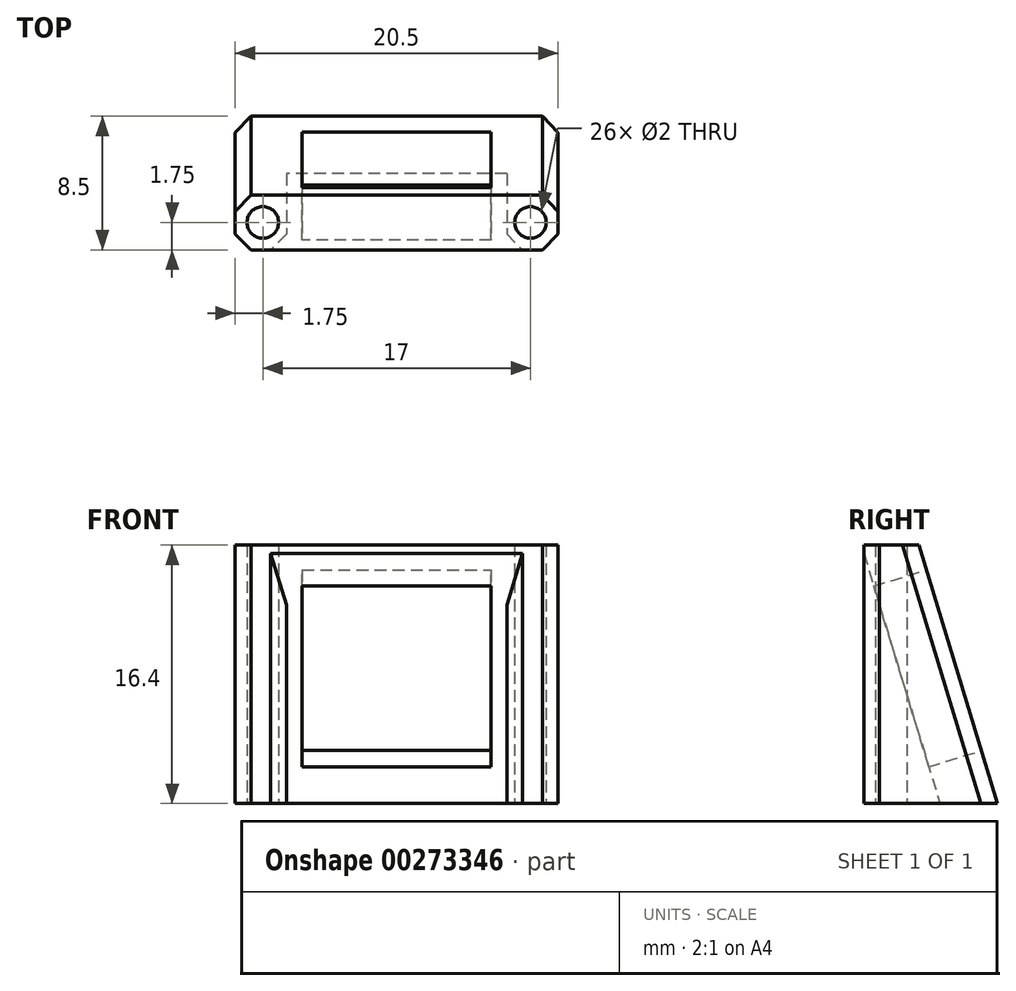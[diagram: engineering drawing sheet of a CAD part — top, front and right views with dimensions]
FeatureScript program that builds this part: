
annotation { "Feature Type Name" : "Feature", "Feature Type Description" : "" }
export const myFeature = defineFeature(function(context is Context, id is Id, definition is map)
    precondition{}
    {
        {
            var Q0;
            Q0=qCreatedBy(makeId("Top.planeOp"),FACE);
            var sketch = newSketch(context, id + "F0", { "sketchPlane" : qUnion([Q0])});
            skLineSegment(sketch, "E0.bottom", {"start": v(10.25, 4.25) * mm, "end": v(-10.25, 4.25) * mm});
            skLineSegment(sketch, "E0.top", {"start": v(10.25, -4.25) * mm, "end": v(-10.25, -4.25) * mm});
            skLineSegment(sketch, "E0.left", {"start": v(10.25, 4.25) * mm, "end": v(10.25, -4.25) * mm});
            skLineSegment(sketch, "E0.right", {"start": v(-10.25, 4.25) * mm, "end": v(-10.25, -4.25) * mm});
            skPoint(sketch, "E0.middle", {"position": v(0, 0) * mm});
            skCircle(sketch, "E1", {"center": v(-8.5, -2.5) * mm, "radius": 1 * mm});
            skCircle(sketch, "E2", {"center": v(8.5, -2.5) * mm, "radius": 1 * mm});
            skLineSegment(sketch, "E3", {"start": v(-8.5, -2.5) * mm, "end": v(8.5, -2.5) * mm});
            skLineSegment(sketch, "E4", {"start": v(0, 0) * mm, "end": v(0, -2.5) * mm});
            skSolve(sketch);
        }
        {
            var Q0;
            Q0=makeQuery(id+"F0.imprint","IMPRINT",FACE,{"disambiguationData":[TD([[makeQuery(id+"F0.imprint","IMPRINT",EDGE,{"derivedFrom":sQuery(id+"F0.wireOp",EDGE,"E0.bottom")}),1.0]])]});
            extrude(context, id + "F1", {"entities" : qUnion([Q0]), "depth" : 16.4 * mm});
        }
        {
            var Q0;
            Q0=makeQuery(id+"F1.opExtrude","CAP_EDGE",EDGE,{"disambiguationData":[OSD([sQuery(id+"F0.wireOp",EDGE,"E0.bottom")])],"isStart":false});
            chamfer(context, id + "F2", {"entities" : qUnion([Q0]), "chamferType" : ChamferType.TWO_OFFSETS, "width1" : 5 * mm, "oppositeDirection" : false, "width2" : 16.4 * mm, "tangentPropagation" : true});
        }
        {
            var Q0;
            Q0=makeQuery(id+"F2.opChamfer","BLEND_FACE",FACE,{"disambiguationData":[OSD([sQuery(id+"F0.wireOp",EDGE,"E0.bottom")])]});
            var sketch = newSketch(context, id + "F3", { "sketchPlane" : qUnion([Q0])});
            skLineSegment(sketch, "E5.bottom", {"start": v(6, 14.26) * mm, "end": v(-6, 14.26) * mm});
            skLineSegment(sketch, "E5.top", {"start": v(6, 2.26) * mm, "end": v(-6, 2.26) * mm});
            skLineSegment(sketch, "E5.left", {"start": v(6, 14.26) * mm, "end": v(6, 2.26) * mm});
            skLineSegment(sketch, "E5.right", {"start": v(-6, 14.26) * mm, "end": v(-6, 2.26) * mm});
            skPoint(sketch, "E5.middle", {"position": v(0, 8.26) * mm});
            skLineSegment(sketch, "E6.0", {"start": v(10.25, 15.9) * mm, "end": v(10.25, -1.24) * mm});
            skSolve(sketch);
        }
        {
            var Q0;
            {var subQ3=sQuery(id+"F3.wireOp",EDGE,"E5.bottom");Q0=makeQuery(id+"F3.imprint","IMPRINT",FACE,{"disambiguationData":[TD([[makeQuery(id+"F3.imprint","IMPRINT",EDGE,{"derivedFrom":subQ3}),1.0]])]});}
            extrude(context, id + "F4", {"entities" : qUnion([Q0]), "operationType" : NewBodyOperationType.REMOVE, "endBound" : BoundingType.THROUGH_ALL, "oppositeDirection" : true, "depth" : 25 * mm});
        }
        {
            var Q0;
            Q0=makeQuery(id+"F2.opChamfer","BLEND_FACE",FACE,{"disambiguationData":[OSD([sQuery(id+"F0.wireOp",EDGE,"E0.bottom")])]});
            cPlane(context, id + "F5", {"entities" : qUnion([Q0]), "cplaneType" : CPlaneType.OFFSET, "offset" : 8.5 * mm, "oppositeDirection" : true, "width" : 150 * mm, "height" : 150 * mm});
        }
        {
            var Q0;
            Q0=qCreatedBy(id+"F5.planeOp",FACE);
            var sketch = newSketch(context, id + "F6", { "sketchPlane" : qUnion([Q0])});
            skLineSegment(sketch, "E7.bottom", {"start": v(7, 18.45) * mm, "end": v(-7, 18.45) * mm});
            skLineSegment(sketch, "E7.top", {"start": v(7, -1.55) * mm, "end": v(-7, -1.55) * mm});
            skLineSegment(sketch, "E7.left", {"start": v(7, 18.45) * mm, "end": v(7, -1.55) * mm});
            skLineSegment(sketch, "E7.right", {"start": v(-7, 18.45) * mm, "end": v(-7, -1.55) * mm});
            skPoint(sketch, "E7.middle", {"position": v(0, 8.45) * mm});
            skSolve(sketch);
        }
        {
            var Q0;
            Q0=makeQuery(id+"F6.imprint","IMPRINT",FACE,{"disambiguationData":[TD([[makeQuery(id+"F6.imprint","IMPRINT",EDGE,{"derivedFrom":sQuery(id+"F6.wireOp",EDGE,"E7.bottom")}),1.0]])]});
            extrude(context, id + "F7", {"entities" : qUnion([Q0]), "operationType" : NewBodyOperationType.REMOVE, "depth" : 5 * mm});
        }
        {
            var Q0;
            Q0=makeQuery(id+"F2.opChamfer","BLEND_EDGE",EDGE,{"blendedFrom":[makeQuery(id+"F1.opExtrude","CAP_EDGE",EDGE,{"disambiguationData":[OSD([sQuery(id+"F0.wireOp",EDGE,"E0.bottom")])],"isStart":false}),makeQuery(id+"F1.opExtrude","SWEPT_FACE",FACE,{"disambiguationData":[OSD([sQuery(id+"F0.wireOp",EDGE,"E0.right")])]})],"blendedInto":[makeQuery(id+"F1.opExtrude","SWEPT_FACE",FACE,{"disambiguationData":[OSD([sQuery(id+"F0.wireOp",EDGE,"E0.right")])]})]});
            var Q1;
            Q1=makeQuery(id+"F1.opExtrude","SWEPT_EDGE",EDGE,{"disambiguationData":[OSD([sQuery(id+"F0.wireOp",EDGE,"E0.top"),sQuery(id+"F0.wireOp",EDGE,"E0.right")])]});
            var Q2;
            Q2=makeQuery(id+"F2.opChamfer","BLEND_EDGE",EDGE,{"blendedFrom":[makeQuery(id+"F1.opExtrude","CAP_EDGE",EDGE,{"disambiguationData":[OSD([sQuery(id+"F0.wireOp",EDGE,"E0.bottom")])],"isStart":false}),makeQuery(id+"F1.opExtrude","SWEPT_FACE",FACE,{"disambiguationData":[OSD([sQuery(id+"F0.wireOp",EDGE,"E0.left")])]})],"blendedInto":[makeQuery(id+"F1.opExtrude","SWEPT_FACE",FACE,{"disambiguationData":[OSD([sQuery(id+"F0.wireOp",EDGE,"E0.left")])]})]});
            var Q3;
            Q3=makeQuery(id+"F1.opExtrude","SWEPT_EDGE",EDGE,{"disambiguationData":[OSD([sQuery(id+"F0.wireOp",EDGE,"E0.top"),sQuery(id+"F0.wireOp",EDGE,"E0.left")])]});
            var Q4;
            Q4=makeQuery(id+"F7.boolean.opBoolean","INTERSECT",EDGE,{"derivedFrom":[makeQuery(id+"F1.opExtrude","SWEPT_FACE",FACE,{"disambiguationData":[OSD([sQuery(id+"F0.wireOp",EDGE,"E0.top")])]}),makeQuery(id+"F7.opExtrude","SWEPT_FACE",FACE,{"disambiguationData":[OSD([sQuery(id+"F6.wireOp",EDGE,"E7.right")])]})]});
            var Q5;
            Q5=makeQuery(id+"F7.boolean.opBoolean","INTERSECT",EDGE,{"derivedFrom":[makeQuery(id+"F1.opExtrude","SWEPT_FACE",FACE,{"disambiguationData":[OSD([sQuery(id+"F0.wireOp",EDGE,"E0.top")])]}),makeQuery(id+"F7.opExtrude","SWEPT_FACE",FACE,{"disambiguationData":[OSD([sQuery(id+"F6.wireOp",EDGE,"E7.left")])]})]});
            chamfer(context, id + "F8", {"entities" : qUnion([Q0, Q1, Q2, Q3, Q4, Q5]), "width" : 1 * mm, "tangentPropagation" : true});
        }
    });
